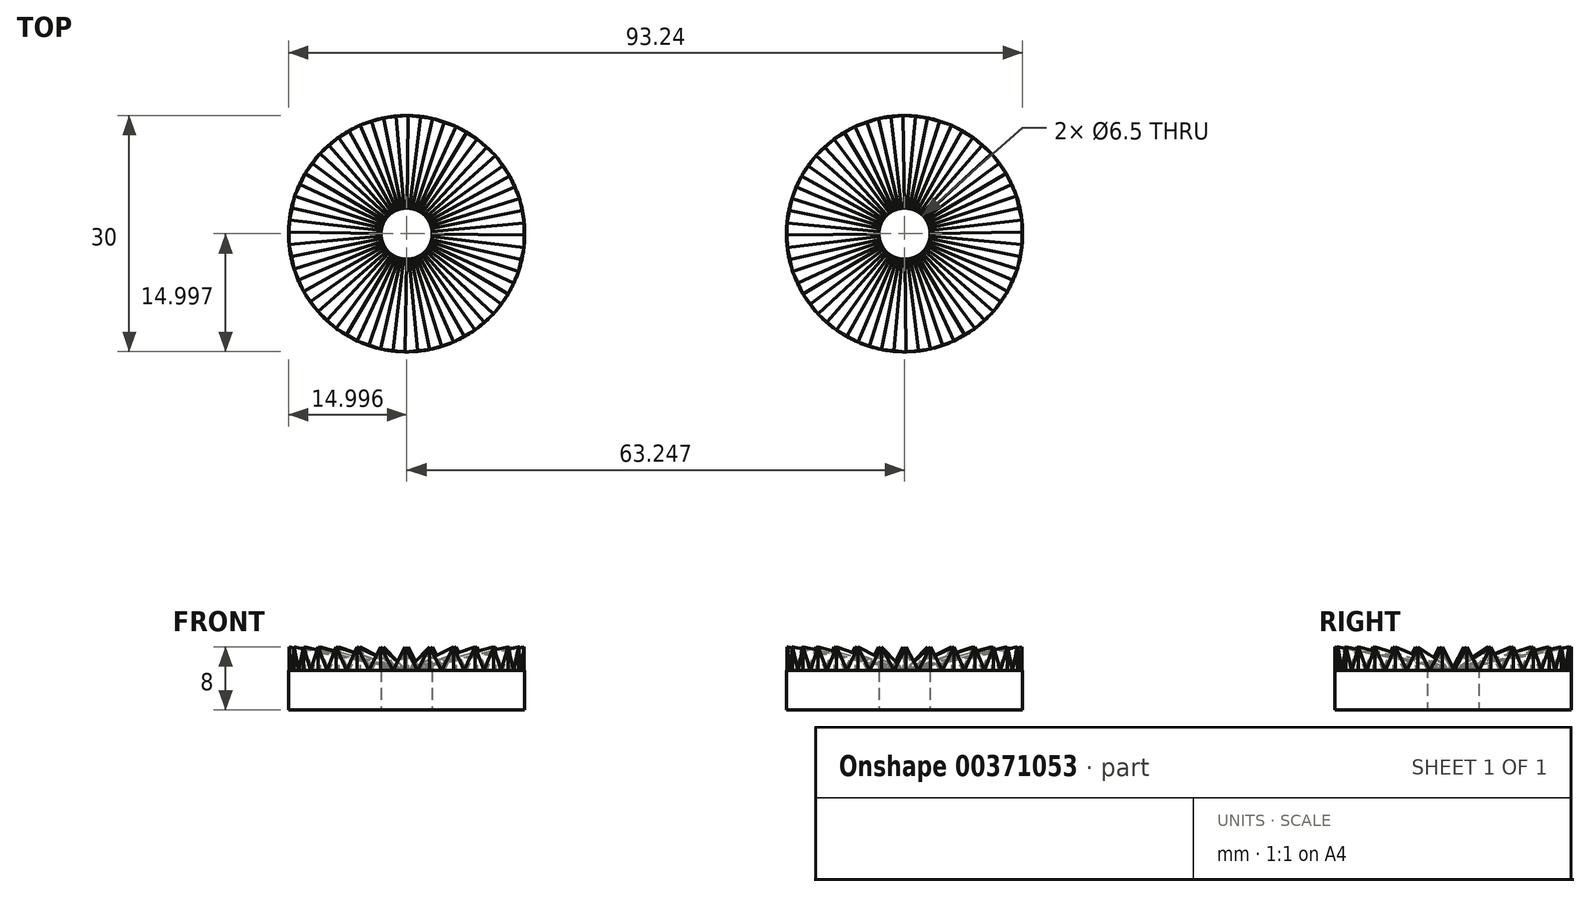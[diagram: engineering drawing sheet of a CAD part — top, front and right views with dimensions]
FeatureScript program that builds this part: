
annotation { "Feature Type Name" : "Feature", "Feature Type Description" : "" }
export const myFeature = defineFeature(function(context is Context, id is Id, definition is map)
    precondition{}
    {
        {
            var Q0;
            Q0=qCreatedBy(makeId("Top.planeOp"),FACE);
            var sketch = newSketch(context, id + "F0", { "sketchPlane" : qUnion([Q0])});
            skCircle(sketch, "E0", {"center": v(31.62, -37.74) * mm, "radius": 15 * mm});
            skSolve(sketch);
        }
        {
            var Q0;
            Q0 = qSketchRegion(id + "F0", true);
            extrude(context, id + "F1", {"entities" : qUnion([Q0]), "depth" : 5 * mm});
        }
        {
            var Q0;
            Q0=makeQuery(id+"F1.opExtrude","CAP_FACE",FACE,{"disambiguationData":[OSD([sQuery(id+"F0.wireOp",EDGE,"E0")])],"isStart":false});
            var sketch = newSketch(context, id + "F2", { "sketchPlane" : qUnion([Q0])});
            skCircle(sketch, "E1.cCircle", {"center": v(31.62, -37.74) * mm, "radius": 15 * mm, "construction": true});
            skLineSegment(sketch, "E1.0", {"start": v(44.7, -45.08) * mm, "end": v(42.9, -47.64) * mm});
            skLineSegment(sketch, "E1.1", {"start": v(42.9, -47.64) * mm, "end": v(40.59, -49.77) * mm});
            skLineSegment(sketch, "E1.2", {"start": v(40.59, -49.77) * mm, "end": v(37.9, -51.37) * mm});
            skLineSegment(sketch, "E1.3", {"start": v(37.9, -51.37) * mm, "end": v(34.92, -52.38) * mm});
            skLineSegment(sketch, "E1.4", {"start": v(34.92, -52.38) * mm, "end": v(31.8, -52.74) * mm});
            skLineSegment(sketch, "E1.5", {"start": v(31.8, -52.74) * mm, "end": v(28.69, -52.45) * mm});
            skLineSegment(sketch, "E1.6", {"start": v(28.69, -52.45) * mm, "end": v(25.7, -51.52) * mm});
            skLineSegment(sketch, "E1.7", {"start": v(25.7, -51.52) * mm, "end": v(22.96, -49.99) * mm});
            skLineSegment(sketch, "E1.8", {"start": v(22.96, -49.99) * mm, "end": v(20.6, -47.92) * mm});
            skLineSegment(sketch, "E1.9", {"start": v(20.6, -47.92) * mm, "end": v(18.73, -45.4) * mm});
            skLineSegment(sketch, "E1.10", {"start": v(18.73, -45.4) * mm, "end": v(17.42, -42.55) * mm});
            skLineSegment(sketch, "E1.11", {"start": v(17.42, -42.55) * mm, "end": v(16.73, -39.5) * mm});
            skLineSegment(sketch, "E1.12", {"start": v(16.73, -39.5) * mm, "end": v(16.69, -36.36) * mm});
            skLineSegment(sketch, "E1.13", {"start": v(16.69, -36.36) * mm, "end": v(17.3, -33.28) * mm});
            skLineSegment(sketch, "E1.14", {"start": v(17.3, -33.28) * mm, "end": v(18.54, -30.4) * mm});
            skLineSegment(sketch, "E1.15", {"start": v(18.54, -30.4) * mm, "end": v(20.35, -27.84) * mm});
            skLineSegment(sketch, "E1.16", {"start": v(20.35, -27.84) * mm, "end": v(22.66, -25.72) * mm});
            skLineSegment(sketch, "E1.17", {"start": v(22.66, -25.72) * mm, "end": v(25.35, -24.12) * mm});
            skLineSegment(sketch, "E1.18", {"start": v(25.35, -24.12) * mm, "end": v(28.32, -23.11) * mm});
            skLineSegment(sketch, "E1.19", {"start": v(28.32, -23.11) * mm, "end": v(31.44, -22.74) * mm});
            skLineSegment(sketch, "E1.20", {"start": v(31.44, -22.74) * mm, "end": v(34.56, -23.03) * mm});
            skLineSegment(sketch, "E1.21", {"start": v(34.56, -23.03) * mm, "end": v(37.56, -23.97) * mm});
            skLineSegment(sketch, "E1.22", {"start": v(37.56, -23.97) * mm, "end": v(40.3, -25.5) * mm});
            skLineSegment(sketch, "E1.23", {"start": v(40.3, -25.5) * mm, "end": v(42.65, -27.57) * mm});
            skLineSegment(sketch, "E1.24", {"start": v(42.65, -27.57) * mm, "end": v(44.52, -30.08) * mm});
            skLineSegment(sketch, "E1.25", {"start": v(44.52, -30.08) * mm, "end": v(45.83, -32.93) * mm});
            skLineSegment(sketch, "E1.26", {"start": v(45.83, -32.93) * mm, "end": v(46.52, -36) * mm});
            skLineSegment(sketch, "E1.27", {"start": v(46.52, -36) * mm, "end": v(46.56, -39.13) * mm});
            skLineSegment(sketch, "E1.28", {"start": v(46.56, -39.13) * mm, "end": v(45.95, -42.2) * mm});
            skLineSegment(sketch, "E1.29", {"start": v(45.95, -42.2) * mm, "end": v(44.7, -45.08) * mm});
            skSolve(sketch);
        }
        {
            var Q0;
            Q0 = qSketchRegion(id + "F2", true);
            extrude(context, id + "F3", {"entities" : qUnion([Q0]), "operationType" : NewBodyOperationType.ADD, "depth" : 3 * mm});
        }
        {
            var Q0;
            Q0=makeQuery(id+"F3.opExtrude","SWEPT_FACE",FACE,{"disambiguationData":[OSD([sQuery(id+"F2.wireOp",EDGE,"E1.22")])]});
            var sketch = newSketch(context, id + "F4", { "sketchPlane" : qUnion([Q0])});
            skLineSegment(sketch, "E2", {"start": v(-44.48, 8) * mm, "end": v(-46.05, 5) * mm});
            skLineSegment(sketch, "E3", {"start": v(-46.05, 5) * mm, "end": v(-47.62, 8) * mm});
            skSolve(sketch);
        }
        {
            var Q0;
            Q0=makeQuery(id+"F3.opExtrude","SWEPT_FACE",FACE,{"disambiguationData":[OSD([sQuery(id+"F2.wireOp",EDGE,"E1.23")])]});
            var sketch = newSketch(context, id + "F5", { "sketchPlane" : qUnion([Q0])});
            skLineSegment(sketch, "E4", {"start": v(-47.1, 8) * mm, "end": v(-48.67, 5) * mm});
            skLineSegment(sketch, "E5", {"start": v(-48.67, 5) * mm, "end": v(-50.24, 8) * mm});
            skSolve(sketch);
        }
        {
            var Q0;
            Q0=makeQuery(id+"F3.opExtrude","SWEPT_FACE",FACE,{"disambiguationData":[OSD([sQuery(id+"F2.wireOp",EDGE,"E1.24")])]});
            var sketch = newSketch(context, id + "F6", { "sketchPlane" : qUnion([Q0])});
            skLineSegment(sketch, "E6", {"start": v(-47.6, 8) * mm, "end": v(-49.16, 5) * mm});
            skLineSegment(sketch, "E7", {"start": v(-49.16, 5) * mm, "end": v(-50.73, 8) * mm});
            skSolve(sketch);
        }
        {
            var Q0;
            Q0=makeQuery(id+"F4.imprint","IMPRINT",FACE,{"disambiguationData":[TD([[makeQuery(id+"F4.imprint","IMPRINT",EDGE,{"derivedFrom":sQuery(id+"F4.wireOp",EDGE,"E2")}),-1.0]])]});
            extrude(context, id + "F7", {"entities" : qUnion([Q0]), "operationType" : NewBodyOperationType.REMOVE, "endBound" : BoundingType.THROUGH_ALL, "oppositeDirection" : true, "depth" : 25 * mm});
        }
        {
            var Q0;
            Q0=makeQuery(id+"F3.opExtrude","SWEPT_FACE",FACE,{"disambiguationData":[OSD([sQuery(id+"F2.wireOp",EDGE,"E1.25")])]});
            var sketch = newSketch(context, id + "F8", { "sketchPlane" : qUnion([Q0])});
            skLineSegment(sketch, "E8", {"start": v(-45.94, 8) * mm, "end": v(-47.5, 5) * mm});
            skLineSegment(sketch, "E9", {"start": v(-47.5, 5) * mm, "end": v(-49.07, 8) * mm});
            skSolve(sketch);
        }
        {
            var Q0;
            Q0=makeQuery(id+"F3.opExtrude","SWEPT_FACE",FACE,{"disambiguationData":[OSD([sQuery(id+"F2.wireOp",EDGE,"E1.26")])]});
            var sketch = newSketch(context, id + "F9", { "sketchPlane" : qUnion([Q0])});
            skLineSegment(sketch, "E10", {"start": v(-42.2, 8) * mm, "end": v(-43.77, 5) * mm});
            skLineSegment(sketch, "E11", {"start": v(-43.77, 5) * mm, "end": v(-45.34, 8) * mm});
            skSolve(sketch);
        }
        {
            var Q0;
            Q0=makeQuery(id+"F3.opExtrude","SWEPT_FACE",FACE,{"disambiguationData":[OSD([sQuery(id+"F2.wireOp",EDGE,"E1.27")])]});
            var sketch = newSketch(context, id + "F10", { "sketchPlane" : qUnion([Q0])});
            skLineSegment(sketch, "E12", {"start": v(-36.56, 8) * mm, "end": v(-38.13, 5) * mm});
            skLineSegment(sketch, "E13", {"start": v(-38.13, 5) * mm, "end": v(-39.7, 8) * mm});
            skSolve(sketch);
        }
        {
            var Q0;
            Q0=makeQuery(id+"F3.opExtrude","SWEPT_FACE",FACE,{"disambiguationData":[OSD([sQuery(id+"F2.wireOp",EDGE,"E1.28")])]});
            var sketch = newSketch(context, id + "F11", { "sketchPlane" : qUnion([Q0])});
            skLineSegment(sketch, "E14", {"start": v(-29.25, 8) * mm, "end": v(-30.82, 5) * mm});
            skLineSegment(sketch, "E15", {"start": v(-30.82, 5) * mm, "end": v(-32.39, 8) * mm});
            skSolve(sketch);
        }
        {
            var Q0;
            Q0=makeQuery(id+"F3.opExtrude","SWEPT_FACE",FACE,{"disambiguationData":[OSD([sQuery(id+"F2.wireOp",EDGE,"E1.29")])]});
            var sketch = newSketch(context, id + "F12", { "sketchPlane" : qUnion([Q0])});
            skLineSegment(sketch, "E16", {"start": v(-20.6, 8) * mm, "end": v(-22.16, 5) * mm});
            skLineSegment(sketch, "E17", {"start": v(-22.16, 5) * mm, "end": v(-23.73, 8) * mm});
            skSolve(sketch);
        }
        {
            var Q0;
            Q0=makeQuery(id+"F3.opExtrude","SWEPT_FACE",FACE,{"disambiguationData":[OSD([sQuery(id+"F2.wireOp",EDGE,"E1.0")])]});
            var sketch = newSketch(context, id + "F13", { "sketchPlane" : qUnion([Q0])});
            skLineSegment(sketch, "E18", {"start": v(-10.97, 8) * mm, "end": v(-12.53, 5) * mm});
            skLineSegment(sketch, "E19", {"start": v(-12.53, 5) * mm, "end": v(-14.1, 8) * mm});
            skSolve(sketch);
        }
        {
            var Q0;
            Q0=makeQuery(id+"F3.opExtrude","SWEPT_FACE",FACE,{"disambiguationData":[OSD([sQuery(id+"F2.wireOp",EDGE,"E1.1")])]});
            var sketch = newSketch(context, id + "F14", { "sketchPlane" : qUnion([Q0])});
            skLineSegment(sketch, "E20", {"start": v(-0.8, 8) * mm, "end": v(-2.36, 5) * mm});
            skLineSegment(sketch, "E21", {"start": v(-2.36, 5) * mm, "end": v(-3.93, 8) * mm});
            skSolve(sketch);
        }
        {
            var Q0;
            Q0=makeQuery(id+"F3.opExtrude","SWEPT_FACE",FACE,{"disambiguationData":[OSD([sQuery(id+"F2.wireOp",EDGE,"E1.2")])]});
            var sketch = newSketch(context, id + "F15", { "sketchPlane" : qUnion([Q0])});
            skLineSegment(sketch, "E22", {"start": v(9.49, 8) * mm, "end": v(7.92, 5) * mm});
            skLineSegment(sketch, "E23", {"start": v(7.92, 5) * mm, "end": v(6.35, 8) * mm});
            skSolve(sketch);
        }
        {
            var Q0;
            Q0=makeQuery(id+"F3.opExtrude","SWEPT_FACE",FACE,{"disambiguationData":[OSD([sQuery(id+"F2.wireOp",EDGE,"E1.3")])]});
            var sketch = newSketch(context, id + "F16", { "sketchPlane" : qUnion([Q0])});
            skLineSegment(sketch, "E24", {"start": v(19.42, 8) * mm, "end": v(17.85, 5) * mm});
            skLineSegment(sketch, "E25", {"start": v(17.85, 5) * mm, "end": v(16.28, 8) * mm});
            skSolve(sketch);
        }
        {
            var Q0;
            Q0=makeQuery(id+"F3.opExtrude","SWEPT_FACE",FACE,{"disambiguationData":[OSD([sQuery(id+"F2.wireOp",EDGE,"E1.4")])]});
            var sketch = newSketch(context, id + "F17", { "sketchPlane" : qUnion([Q0])});
            skLineSegment(sketch, "E26", {"start": v(28.57, 8) * mm, "end": v(27, 5) * mm});
            skLineSegment(sketch, "E27", {"start": v(27, 5) * mm, "end": v(25.43, 8) * mm});
            skSolve(sketch);
        }
        {
            var Q0;
            Q0=makeQuery(id+"F3.opExtrude","SWEPT_FACE",FACE,{"disambiguationData":[OSD([sQuery(id+"F2.wireOp",EDGE,"E1.5")])]});
            var sketch = newSketch(context, id + "F18", { "sketchPlane" : qUnion([Q0])});
            skLineSegment(sketch, "E28", {"start": v(36.54, 8) * mm, "end": v(34.97, 5) * mm});
            skLineSegment(sketch, "E29", {"start": v(34.97, 5) * mm, "end": v(33.4, 8) * mm});
            skSolve(sketch);
        }
        {
            var Q0;
            Q0=makeQuery(id+"F3.opExtrude","SWEPT_FACE",FACE,{"disambiguationData":[OSD([sQuery(id+"F2.wireOp",EDGE,"E1.6")])]});
            var sketch = newSketch(context, id + "F19", { "sketchPlane" : qUnion([Q0])});
            skLineSegment(sketch, "E30", {"start": v(42.98, 8) * mm, "end": v(41.41, 5) * mm});
            skLineSegment(sketch, "E31", {"start": v(41.41, 5) * mm, "end": v(39.85, 8) * mm});
            skSolve(sketch);
        }
        {
            var Q0;
            Q0=makeQuery(id+"F5.imprint","IMPRINT",FACE,{"disambiguationData":[TD([[makeQuery(id+"F5.imprint","IMPRINT",EDGE,{"derivedFrom":sQuery(id+"F5.wireOp",EDGE,"E4")}),-1.0]])]});
            extrude(context, id + "F20", {"entities" : qUnion([Q0]), "operationType" : NewBodyOperationType.REMOVE, "endBound" : BoundingType.THROUGH_ALL, "oppositeDirection" : true, "depth" : 25 * mm});
        }
        {
            var Q0;
            Q0=makeQuery(id+"F6.imprint","IMPRINT",FACE,{"disambiguationData":[TD([[makeQuery(id+"F6.imprint","IMPRINT",EDGE,{"derivedFrom":sQuery(id+"F6.wireOp",EDGE,"E6")}),-1.0]])]});
            extrude(context, id + "F21", {"entities" : qUnion([Q0]), "operationType" : NewBodyOperationType.REMOVE, "endBound" : BoundingType.THROUGH_ALL, "oppositeDirection" : true, "depth" : 25 * mm});
        }
        {
            var Q0;
            Q0=makeQuery(id+"F8.imprint","IMPRINT",FACE,{"disambiguationData":[TD([[makeQuery(id+"F8.imprint","IMPRINT",EDGE,{"derivedFrom":sQuery(id+"F8.wireOp",EDGE,"E8")}),-1.0]])]});
            extrude(context, id + "F22", {"entities" : qUnion([Q0]), "operationType" : NewBodyOperationType.REMOVE, "endBound" : BoundingType.THROUGH_ALL, "oppositeDirection" : true, "depth" : 25 * mm});
        }
        {
            var Q0;
            Q0=makeQuery(id+"F9.imprint","IMPRINT",FACE,{"disambiguationData":[TD([[makeQuery(id+"F9.imprint","IMPRINT",EDGE,{"derivedFrom":sQuery(id+"F9.wireOp",EDGE,"E10")}),-1.0]])]});
            extrude(context, id + "F23", {"entities" : qUnion([Q0]), "operationType" : NewBodyOperationType.REMOVE, "endBound" : BoundingType.THROUGH_ALL, "oppositeDirection" : true, "depth" : 25 * mm});
        }
        {
            var Q0;
            Q0=makeQuery(id+"F10.imprint","IMPRINT",FACE,{"disambiguationData":[TD([[makeQuery(id+"F10.imprint","IMPRINT",EDGE,{"derivedFrom":sQuery(id+"F10.wireOp",EDGE,"E12")}),-1.0]])]});
            extrude(context, id + "F24", {"entities" : qUnion([Q0]), "operationType" : NewBodyOperationType.REMOVE, "endBound" : BoundingType.THROUGH_ALL, "oppositeDirection" : true, "depth" : 25 * mm});
        }
        {
            var Q0;
            Q0=makeQuery(id+"F11.imprint","IMPRINT",FACE,{"disambiguationData":[TD([[makeQuery(id+"F11.imprint","IMPRINT",EDGE,{"derivedFrom":sQuery(id+"F11.wireOp",EDGE,"E14")}),-1.0]])]});
            extrude(context, id + "F25", {"entities" : qUnion([Q0]), "operationType" : NewBodyOperationType.REMOVE, "endBound" : BoundingType.THROUGH_ALL, "oppositeDirection" : true, "depth" : 25 * mm});
        }
        {
            var Q0;
            Q0=makeQuery(id+"F12.imprint","IMPRINT",FACE,{"disambiguationData":[TD([[makeQuery(id+"F12.imprint","IMPRINT",EDGE,{"derivedFrom":sQuery(id+"F12.wireOp",EDGE,"E16")}),-1.0]])]});
            extrude(context, id + "F26", {"entities" : qUnion([Q0]), "operationType" : NewBodyOperationType.REMOVE, "endBound" : BoundingType.THROUGH_ALL, "oppositeDirection" : true, "depth" : 25 * mm});
        }
        {
            var Q0;
            Q0=makeQuery(id+"F13.imprint","IMPRINT",FACE,{"disambiguationData":[TD([[makeQuery(id+"F13.imprint","IMPRINT",EDGE,{"derivedFrom":sQuery(id+"F13.wireOp",EDGE,"E18")}),-1.0]])]});
            extrude(context, id + "F27", {"entities" : qUnion([Q0]), "operationType" : NewBodyOperationType.REMOVE, "endBound" : BoundingType.THROUGH_ALL, "oppositeDirection" : true, "depth" : 25 * mm});
        }
        {
            var Q0;
            Q0=makeQuery(id+"F14.imprint","IMPRINT",FACE,{"disambiguationData":[TD([[makeQuery(id+"F14.imprint","IMPRINT",EDGE,{"derivedFrom":sQuery(id+"F14.wireOp",EDGE,"E20")}),-1.0]])]});
            extrude(context, id + "F28", {"entities" : qUnion([Q0]), "operationType" : NewBodyOperationType.REMOVE, "endBound" : BoundingType.THROUGH_ALL, "oppositeDirection" : true, "depth" : 25 * mm});
        }
        {
            var Q0;
            Q0=makeQuery(id+"F15.imprint","IMPRINT",FACE,{"disambiguationData":[TD([[makeQuery(id+"F15.imprint","IMPRINT",EDGE,{"derivedFrom":sQuery(id+"F15.wireOp",EDGE,"E22")}),-1.0]])]});
            extrude(context, id + "F29", {"entities" : qUnion([Q0]), "operationType" : NewBodyOperationType.REMOVE, "endBound" : BoundingType.THROUGH_ALL, "oppositeDirection" : true, "depth" : 25 * mm});
        }
        {
            var Q0;
            Q0=makeQuery(id+"F16.imprint","IMPRINT",FACE,{"disambiguationData":[TD([[makeQuery(id+"F16.imprint","IMPRINT",EDGE,{"derivedFrom":sQuery(id+"F16.wireOp",EDGE,"E24")}),-1.0]])]});
            extrude(context, id + "F30", {"entities" : qUnion([Q0]), "operationType" : NewBodyOperationType.REMOVE, "endBound" : BoundingType.THROUGH_ALL, "oppositeDirection" : true, "depth" : 25 * mm});
        }
        {
            var Q0;
            Q0=makeQuery(id+"F17.imprint","IMPRINT",FACE,{"disambiguationData":[TD([[makeQuery(id+"F17.imprint","IMPRINT",EDGE,{"derivedFrom":sQuery(id+"F17.wireOp",EDGE,"E26")}),-1.0]])]});
            extrude(context, id + "F31", {"entities" : qUnion([Q0]), "operationType" : NewBodyOperationType.REMOVE, "endBound" : BoundingType.THROUGH_ALL, "oppositeDirection" : true, "depth" : 25 * mm});
        }
        {
            var Q0;
            Q0=makeQuery(id+"F18.imprint","IMPRINT",FACE,{"disambiguationData":[TD([[makeQuery(id+"F18.imprint","IMPRINT",EDGE,{"derivedFrom":sQuery(id+"F18.wireOp",EDGE,"E28")}),-1.0]])]});
            extrude(context, id + "F32", {"entities" : qUnion([Q0]), "operationType" : NewBodyOperationType.REMOVE, "endBound" : BoundingType.THROUGH_ALL, "oppositeDirection" : true, "depth" : 25 * mm});
        }
        {
            var Q0;
            Q0=makeQuery(id+"F19.imprint","IMPRINT",FACE,{"disambiguationData":[TD([[makeQuery(id+"F19.imprint","IMPRINT",EDGE,{"derivedFrom":sQuery(id+"F19.wireOp",EDGE,"E30")}),-1.0]])]});
            extrude(context, id + "F33", {"entities" : qUnion([Q0]), "operationType" : NewBodyOperationType.REMOVE, "endBound" : BoundingType.THROUGH_ALL, "oppositeDirection" : true, "depth" : 25 * mm});
        }
        {
            var Q0;
            Q0=makeQuery(id+"F1.opExtrude","CAP_FACE",FACE,{"disambiguationData":[OSD([sQuery(id+"F0.wireOp",EDGE,"E0")])],"isStart":true});
            var sketch = newSketch(context, id + "F34", { "sketchPlane" : qUnion([Q0])});
            skCircle(sketch, "E32", {"center": v(31.62, 37.74) * mm, "radius": 3.25 * mm});
            skSolve(sketch);
        }
        {
            var Q0;
            Q0 = qSketchRegion(id + "F34", true);
            extrude(context, id + "F35", {"entities" : qUnion([Q0]), "operationType" : NewBodyOperationType.REMOVE, "endBound" : BoundingType.THROUGH_ALL, "oppositeDirection" : true, "depth" : 25 * mm});
        }
        {
            var Q0;
            Q0=makeQuery(id+"F1.opExtrude","SWEPT_BODY",BODY,{"disambiguationData":[OSD([sQuery(id+"F0.wireOp",EDGE,"E0")])]});
            var Q1;
            Q1=qCreatedBy(makeId("Right.planeOp"),FACE);
            mirror(context, id + "F36", {"entities" : qUnion([Q0]), "mirrorPlane" : qUnion([Q1])});
        }
    });
